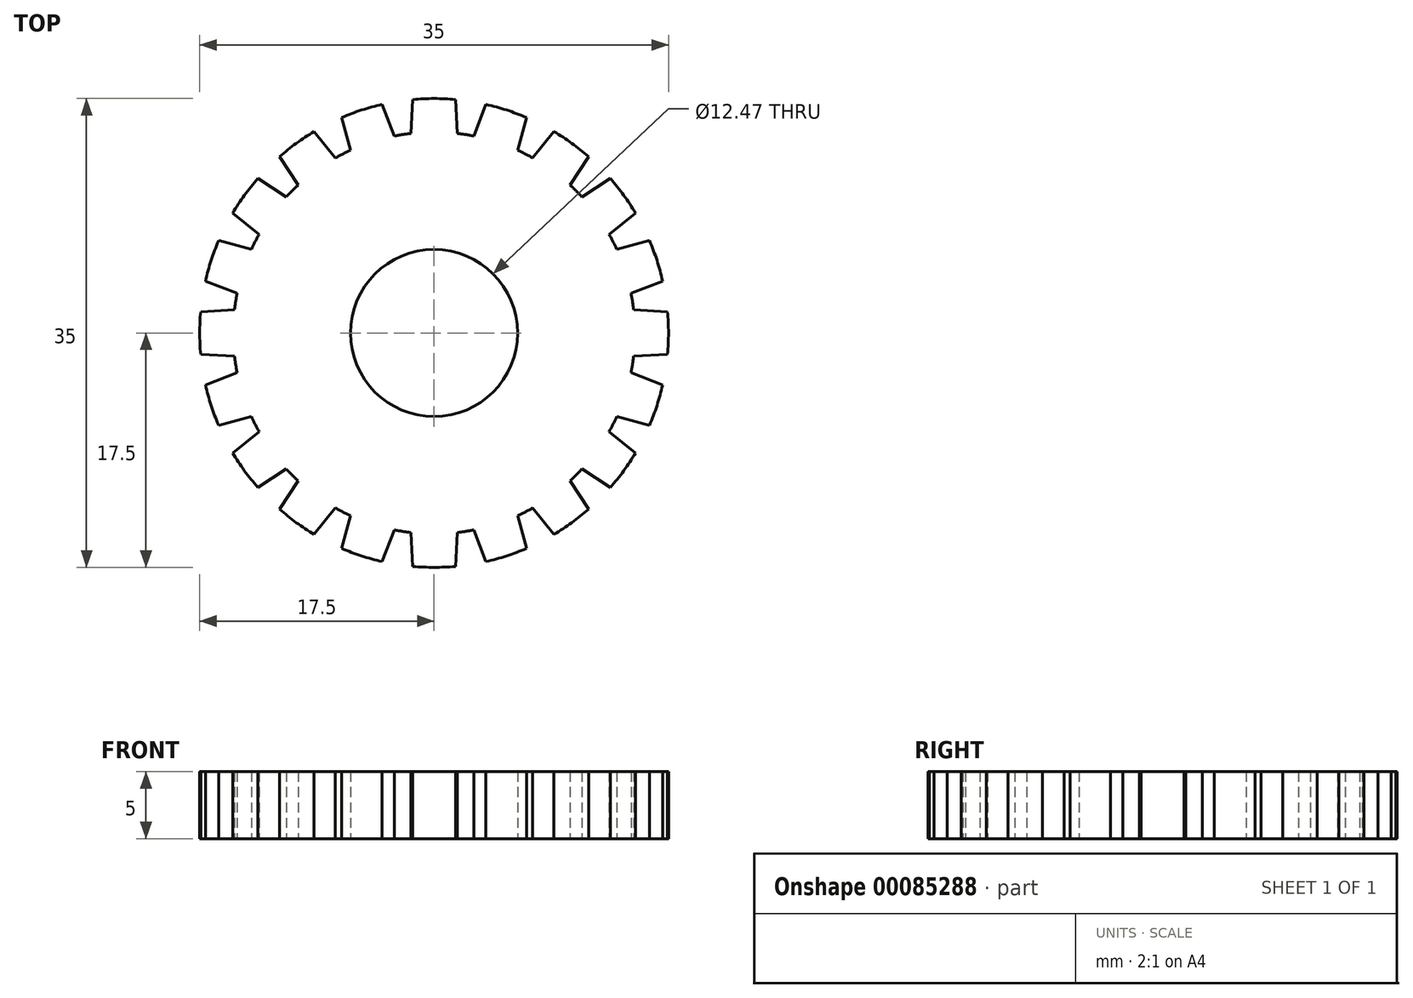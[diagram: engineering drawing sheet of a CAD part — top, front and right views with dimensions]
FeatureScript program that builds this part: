
annotation { "Feature Type Name" : "Feature", "Feature Type Description" : "" }
export const myFeature = defineFeature(function(context is Context, id is Id, definition is map)
    precondition{}
    {
        {
            var Q0;
            Q0=qCreatedBy(makeId("Top.planeOp"),FACE);
            var sketch = newSketch(context, id + "F0", { "sketchPlane" : qUnion([Q0])});
            skCircle(sketch, "E0", {"center": v(0, 0) * mm, "radius": 15 * mm, "construction": true});
            skCircle(sketch, "E1", {"center": v(0, 0) * mm, "radius": 17.5 * mm, "construction": true});
            skLineSegment(sketch, "E2", {"start": v(0, 0) * mm, "end": v(2.35, 14.82) * mm, "construction": true});
            skLineSegment(sketch, "E3.MirrorCS", {"start": v(0, 0) * mm, "end": v(-2.35, 14.82) * mm, "construction": true});
            skLineSegment(sketch, "E4", {"start": v(-1.72, 14.9) * mm, "end": v(-1.6, 17.43) * mm});
            skLineSegment(sketch, "E5.MirrorCS", {"start": v(1.72, 14.9) * mm, "end": v(1.6, 17.43) * mm});
            skArc(sketch, "E6", {"start": v(-1.6, 17.43) * mm, "mid": v(0, 17.5) * mm, "end": v(1.6, 17.43) * mm});
            skArc(sketch, "E7", {"start": v(-2.35, 14.82) * mm, "mid": v(-2.04, 14.86) * mm, "end": v(-1.72, 14.9) * mm});
            skArc(sketch, "E8.MirrorCS", {"start": v(2.35, 14.82) * mm, "mid": v(2.04, 14.86) * mm, "end": v(1.72, 14.9) * mm});
            skLineSegment(sketch, "E9", {"start": v(-1.72, 14.9) * mm, "end": v(0, 0) * mm, "construction": true});
            skArc(sketch, "E10.1.0", {"start": v(-6.8, 13.37) * mm, "mid": v(-6.53, 13.5) * mm, "end": v(-6.24, 13.64) * mm});
            skLineSegment(sketch, "E10.1.1", {"start": v(-6.24, 13.64) * mm, "end": v(-6.9, 16.08) * mm});
            skArc(sketch, "E10.1.2", {"start": v(-6.9, 16.08) * mm, "mid": v(-5.4, 16.64) * mm, "end": v(-3.87, 17.07) * mm});
            skLineSegment(sketch, "E10.1.3", {"start": v(-2.96, 14.7) * mm, "end": v(-3.87, 17.07) * mm});
            skArc(sketch, "E10.1.4", {"start": v(-2.35, 14.82) * mm, "mid": v(-2.66, 14.76) * mm, "end": v(-2.96, 14.7) * mm});
            skArc(sketch, "E10.2.0", {"start": v(-10.6, 10.6) * mm, "mid": v(-10.38, 10.83) * mm, "end": v(-10.15, 11.04) * mm});
            skLineSegment(sketch, "E10.2.1", {"start": v(-10.15, 11.04) * mm, "end": v(-11.53, 13.16) * mm});
            skArc(sketch, "E10.2.2", {"start": v(-11.53, 13.16) * mm, "mid": v(-10.29, 14.16) * mm, "end": v(-8.96, 15.03) * mm});
            skLineSegment(sketch, "E10.2.3", {"start": v(-7.36, 13.07) * mm, "end": v(-8.96, 15.03) * mm});
            skArc(sketch, "E10.2.4", {"start": v(-6.8, 13.37) * mm, "mid": v(-7.09, 13.22) * mm, "end": v(-7.36, 13.07) * mm});
            skArc(sketch, "E10.3.0", {"start": v(-13.37, 6.8) * mm, "mid": v(-13.22, 7.09) * mm, "end": v(-13.07, 7.36) * mm});
            skLineSegment(sketch, "E10.3.1", {"start": v(-13.07, 7.36) * mm, "end": v(-15.03, 8.96) * mm});
            skArc(sketch, "E10.3.2", {"start": v(-15.03, 8.96) * mm, "mid": v(-14.16, 10.29) * mm, "end": v(-13.16, 11.53) * mm});
            skLineSegment(sketch, "E10.3.3", {"start": v(-11.04, 10.15) * mm, "end": v(-13.16, 11.53) * mm});
            skArc(sketch, "E10.3.4", {"start": v(-10.6, 10.6) * mm, "mid": v(-10.83, 10.38) * mm, "end": v(-11.04, 10.15) * mm});
            skArc(sketch, "E10.4.0", {"start": v(-14.82, 2.35) * mm, "mid": v(-14.76, 2.66) * mm, "end": v(-14.7, 2.96) * mm});
            skLineSegment(sketch, "E10.4.1", {"start": v(-14.7, 2.96) * mm, "end": v(-17.07, 3.87) * mm});
            skArc(sketch, "E10.4.2", {"start": v(-17.07, 3.87) * mm, "mid": v(-16.64, 5.4) * mm, "end": v(-16.08, 6.9) * mm});
            skLineSegment(sketch, "E10.4.3", {"start": v(-13.64, 6.24) * mm, "end": v(-16.08, 6.9) * mm});
            skArc(sketch, "E10.4.4", {"start": v(-13.37, 6.8) * mm, "mid": v(-13.5, 6.53) * mm, "end": v(-13.64, 6.24) * mm});
            skArc(sketch, "E10.5.0", {"start": v(-14.82, -2.35) * mm, "mid": v(-14.86, -2.04) * mm, "end": v(-14.9, -1.72) * mm});
            skLineSegment(sketch, "E10.5.1", {"start": v(-14.9, -1.72) * mm, "end": v(-17.43, -1.6) * mm});
            skArc(sketch, "E10.5.2", {"start": v(-17.43, -1.6) * mm, "mid": v(-17.5, 0) * mm, "end": v(-17.43, 1.6) * mm});
            skLineSegment(sketch, "E10.5.3", {"start": v(-14.9, 1.72) * mm, "end": v(-17.43, 1.6) * mm});
            skArc(sketch, "E10.5.4", {"start": v(-14.82, 2.35) * mm, "mid": v(-14.86, 2.04) * mm, "end": v(-14.9, 1.72) * mm});
            skArc(sketch, "E10.6.0", {"start": v(-13.37, -6.8) * mm, "mid": v(-13.5, -6.53) * mm, "end": v(-13.64, -6.24) * mm});
            skLineSegment(sketch, "E10.6.1", {"start": v(-13.64, -6.24) * mm, "end": v(-16.08, -6.9) * mm});
            skArc(sketch, "E10.6.2", {"start": v(-16.08, -6.9) * mm, "mid": v(-16.64, -5.4) * mm, "end": v(-17.07, -3.87) * mm});
            skLineSegment(sketch, "E10.6.3", {"start": v(-14.7, -2.96) * mm, "end": v(-17.07, -3.87) * mm});
            skArc(sketch, "E10.6.4", {"start": v(-14.82, -2.35) * mm, "mid": v(-14.76, -2.66) * mm, "end": v(-14.7, -2.96) * mm});
            skArc(sketch, "E10.7.0", {"start": v(-10.6, -10.6) * mm, "mid": v(-10.83, -10.38) * mm, "end": v(-11.04, -10.15) * mm});
            skLineSegment(sketch, "E10.7.1", {"start": v(-11.04, -10.15) * mm, "end": v(-13.16, -11.53) * mm});
            skArc(sketch, "E10.7.2", {"start": v(-13.16, -11.53) * mm, "mid": v(-14.16, -10.29) * mm, "end": v(-15.03, -8.96) * mm});
            skLineSegment(sketch, "E10.7.3", {"start": v(-13.07, -7.36) * mm, "end": v(-15.03, -8.96) * mm});
            skArc(sketch, "E10.7.4", {"start": v(-13.37, -6.8) * mm, "mid": v(-13.22, -7.09) * mm, "end": v(-13.07, -7.36) * mm});
            skArc(sketch, "E10.8.0", {"start": v(-6.8, -13.37) * mm, "mid": v(-7.09, -13.22) * mm, "end": v(-7.36, -13.07) * mm});
            skLineSegment(sketch, "E10.8.1", {"start": v(-7.36, -13.07) * mm, "end": v(-8.96, -15.03) * mm});
            skArc(sketch, "E10.8.2", {"start": v(-8.96, -15.03) * mm, "mid": v(-10.29, -14.16) * mm, "end": v(-11.53, -13.16) * mm});
            skLineSegment(sketch, "E10.8.3", {"start": v(-10.15, -11.04) * mm, "end": v(-11.53, -13.16) * mm});
            skArc(sketch, "E10.8.4", {"start": v(-10.6, -10.6) * mm, "mid": v(-10.38, -10.83) * mm, "end": v(-10.15, -11.04) * mm});
            skArc(sketch, "E10.9.0", {"start": v(-2.35, -14.82) * mm, "mid": v(-2.66, -14.76) * mm, "end": v(-2.96, -14.7) * mm});
            skLineSegment(sketch, "E10.9.1", {"start": v(-2.96, -14.7) * mm, "end": v(-3.87, -17.07) * mm});
            skArc(sketch, "E10.9.2", {"start": v(-3.87, -17.07) * mm, "mid": v(-5.4, -16.64) * mm, "end": v(-6.9, -16.08) * mm});
            skLineSegment(sketch, "E10.9.3", {"start": v(-6.24, -13.64) * mm, "end": v(-6.9, -16.08) * mm});
            skArc(sketch, "E10.9.4", {"start": v(-6.8, -13.37) * mm, "mid": v(-6.53, -13.5) * mm, "end": v(-6.24, -13.64) * mm});
            skArc(sketch, "E11.1.10.0", {"start": v(2.35, -14.82) * mm, "mid": v(2.04, -14.86) * mm, "end": v(1.72, -14.9) * mm});
            skLineSegment(sketch, "E11.4.10.0", {"start": v(1.72, -14.9) * mm, "end": v(1.6, -17.43) * mm});
            skArc(sketch, "E11.7.10.0", {"start": v(1.6, -17.43) * mm, "mid": v(0, -17.5) * mm, "end": v(-1.6, -17.43) * mm});
            skLineSegment(sketch, "E11.11.10.0", {"start": v(-1.72, -14.9) * mm, "end": v(-1.6, -17.43) * mm});
            skArc(sketch, "E11.14.10.0", {"start": v(-2.35, -14.82) * mm, "mid": v(-2.04, -14.86) * mm, "end": v(-1.72, -14.9) * mm});
            skArc(sketch, "E11.1.11.0", {"start": v(6.8, -13.37) * mm, "mid": v(6.53, -13.5) * mm, "end": v(6.24, -13.64) * mm});
            skLineSegment(sketch, "E11.4.11.0", {"start": v(6.24, -13.64) * mm, "end": v(6.9, -16.08) * mm});
            skArc(sketch, "E11.7.11.0", {"start": v(6.9, -16.08) * mm, "mid": v(5.4, -16.64) * mm, "end": v(3.87, -17.07) * mm});
            skLineSegment(sketch, "E11.11.11.0", {"start": v(2.96, -14.7) * mm, "end": v(3.87, -17.07) * mm});
            skArc(sketch, "E11.14.11.0", {"start": v(2.35, -14.82) * mm, "mid": v(2.66, -14.76) * mm, "end": v(2.96, -14.7) * mm});
            skArc(sketch, "E11.1.12.0", {"start": v(10.6, -10.6) * mm, "mid": v(10.38, -10.83) * mm, "end": v(10.15, -11.04) * mm});
            skLineSegment(sketch, "E11.4.12.0", {"start": v(10.15, -11.04) * mm, "end": v(11.53, -13.16) * mm});
            skArc(sketch, "E11.7.12.0", {"start": v(11.53, -13.16) * mm, "mid": v(10.29, -14.16) * mm, "end": v(8.96, -15.03) * mm});
            skLineSegment(sketch, "E11.11.12.0", {"start": v(7.36, -13.07) * mm, "end": v(8.96, -15.03) * mm});
            skArc(sketch, "E11.14.12.0", {"start": v(6.8, -13.37) * mm, "mid": v(7.09, -13.22) * mm, "end": v(7.36, -13.07) * mm});
            skArc(sketch, "E11.1.13.0", {"start": v(13.37, -6.8) * mm, "mid": v(13.22, -7.09) * mm, "end": v(13.07, -7.36) * mm});
            skLineSegment(sketch, "E11.4.13.0", {"start": v(13.07, -7.36) * mm, "end": v(15.03, -8.96) * mm});
            skArc(sketch, "E11.7.13.0", {"start": v(15.03, -8.96) * mm, "mid": v(14.16, -10.29) * mm, "end": v(13.16, -11.53) * mm});
            skLineSegment(sketch, "E11.11.13.0", {"start": v(11.04, -10.15) * mm, "end": v(13.16, -11.53) * mm});
            skArc(sketch, "E11.14.13.0", {"start": v(10.6, -10.6) * mm, "mid": v(10.83, -10.38) * mm, "end": v(11.04, -10.15) * mm});
            skArc(sketch, "E11.1.14.0", {"start": v(14.82, -2.35) * mm, "mid": v(14.76, -2.66) * mm, "end": v(14.7, -2.96) * mm});
            skLineSegment(sketch, "E11.4.14.0", {"start": v(14.7, -2.96) * mm, "end": v(17.07, -3.87) * mm});
            skArc(sketch, "E11.7.14.0", {"start": v(17.07, -3.87) * mm, "mid": v(16.64, -5.4) * mm, "end": v(16.08, -6.9) * mm});
            skLineSegment(sketch, "E11.11.14.0", {"start": v(13.64, -6.24) * mm, "end": v(16.08, -6.9) * mm});
            skArc(sketch, "E11.14.14.0", {"start": v(13.37, -6.8) * mm, "mid": v(13.5, -6.53) * mm, "end": v(13.64, -6.24) * mm});
            skArc(sketch, "E11.1.15.0", {"start": v(14.82, 2.35) * mm, "mid": v(14.86, 2.04) * mm, "end": v(14.9, 1.72) * mm});
            skLineSegment(sketch, "E11.4.15.0", {"start": v(14.9, 1.72) * mm, "end": v(17.43, 1.6) * mm});
            skArc(sketch, "E11.7.15.0", {"start": v(17.43, 1.6) * mm, "mid": v(17.5, 0) * mm, "end": v(17.43, -1.6) * mm});
            skLineSegment(sketch, "E11.11.15.0", {"start": v(14.9, -1.72) * mm, "end": v(17.43, -1.6) * mm});
            skArc(sketch, "E11.14.15.0", {"start": v(14.82, -2.35) * mm, "mid": v(14.86, -2.04) * mm, "end": v(14.9, -1.72) * mm});
            skArc(sketch, "E11.1.16.0", {"start": v(13.37, 6.8) * mm, "mid": v(13.5, 6.53) * mm, "end": v(13.64, 6.24) * mm});
            skLineSegment(sketch, "E11.4.16.0", {"start": v(13.64, 6.24) * mm, "end": v(16.08, 6.9) * mm});
            skArc(sketch, "E11.7.16.0", {"start": v(16.08, 6.9) * mm, "mid": v(16.64, 5.4) * mm, "end": v(17.07, 3.87) * mm});
            skLineSegment(sketch, "E11.11.16.0", {"start": v(14.7, 2.96) * mm, "end": v(17.07, 3.87) * mm});
            skArc(sketch, "E11.14.16.0", {"start": v(14.82, 2.35) * mm, "mid": v(14.76, 2.66) * mm, "end": v(14.7, 2.96) * mm});
            skArc(sketch, "E11.1.17.0", {"start": v(10.6, 10.6) * mm, "mid": v(10.83, 10.38) * mm, "end": v(11.04, 10.15) * mm});
            skLineSegment(sketch, "E11.4.17.0", {"start": v(11.04, 10.15) * mm, "end": v(13.16, 11.53) * mm});
            skArc(sketch, "E11.7.17.0", {"start": v(13.16, 11.53) * mm, "mid": v(14.16, 10.29) * mm, "end": v(15.03, 8.96) * mm});
            skLineSegment(sketch, "E11.11.17.0", {"start": v(13.07, 7.36) * mm, "end": v(15.03, 8.96) * mm});
            skArc(sketch, "E11.14.17.0", {"start": v(13.37, 6.8) * mm, "mid": v(13.22, 7.09) * mm, "end": v(13.07, 7.36) * mm});
            skArc(sketch, "E11.1.18.0", {"start": v(6.8, 13.37) * mm, "mid": v(7.09, 13.22) * mm, "end": v(7.36, 13.07) * mm});
            skLineSegment(sketch, "E11.4.18.0", {"start": v(7.36, 13.07) * mm, "end": v(8.96, 15.03) * mm});
            skArc(sketch, "E11.7.18.0", {"start": v(8.96, 15.03) * mm, "mid": v(10.29, 14.16) * mm, "end": v(11.53, 13.16) * mm});
            skLineSegment(sketch, "E11.11.18.0", {"start": v(10.15, 11.04) * mm, "end": v(11.53, 13.16) * mm});
            skArc(sketch, "E11.14.18.0", {"start": v(10.6, 10.6) * mm, "mid": v(10.38, 10.83) * mm, "end": v(10.15, 11.04) * mm});
            skArc(sketch, "E11.1.19.0", {"start": v(2.35, 14.82) * mm, "mid": v(2.66, 14.76) * mm, "end": v(2.96, 14.7) * mm});
            skLineSegment(sketch, "E11.4.19.0", {"start": v(2.96, 14.7) * mm, "end": v(3.87, 17.07) * mm});
            skArc(sketch, "E11.7.19.0", {"start": v(3.87, 17.07) * mm, "mid": v(5.4, 16.64) * mm, "end": v(6.9, 16.08) * mm});
            skLineSegment(sketch, "E11.11.19.0", {"start": v(6.24, 13.64) * mm, "end": v(6.9, 16.08) * mm});
            skArc(sketch, "E11.14.19.0", {"start": v(6.8, 13.37) * mm, "mid": v(6.53, 13.5) * mm, "end": v(6.24, 13.64) * mm});
            skCircle(sketch, "E12", {"center": v(0, 0) * mm, "radius": 6.24 * mm});
            skSolve(sketch);
        }
        {
            var Q0;
            Q0=makeQuery(id+"F0.imprint","IMPRINT",FACE,{"disambiguationData":[TD([[makeQuery(id+"F0.imprint","IMPRINT",EDGE,{"derivedFrom":sQuery(id+"F0.wireOp",EDGE,"E4")}),-1.0]])]});
            extrude(context, id + "F1", {"entities" : qUnion([Q0]), "endBound" : BoundingType.SYMMETRIC, "depth" : 5 * mm});
        }
    });
